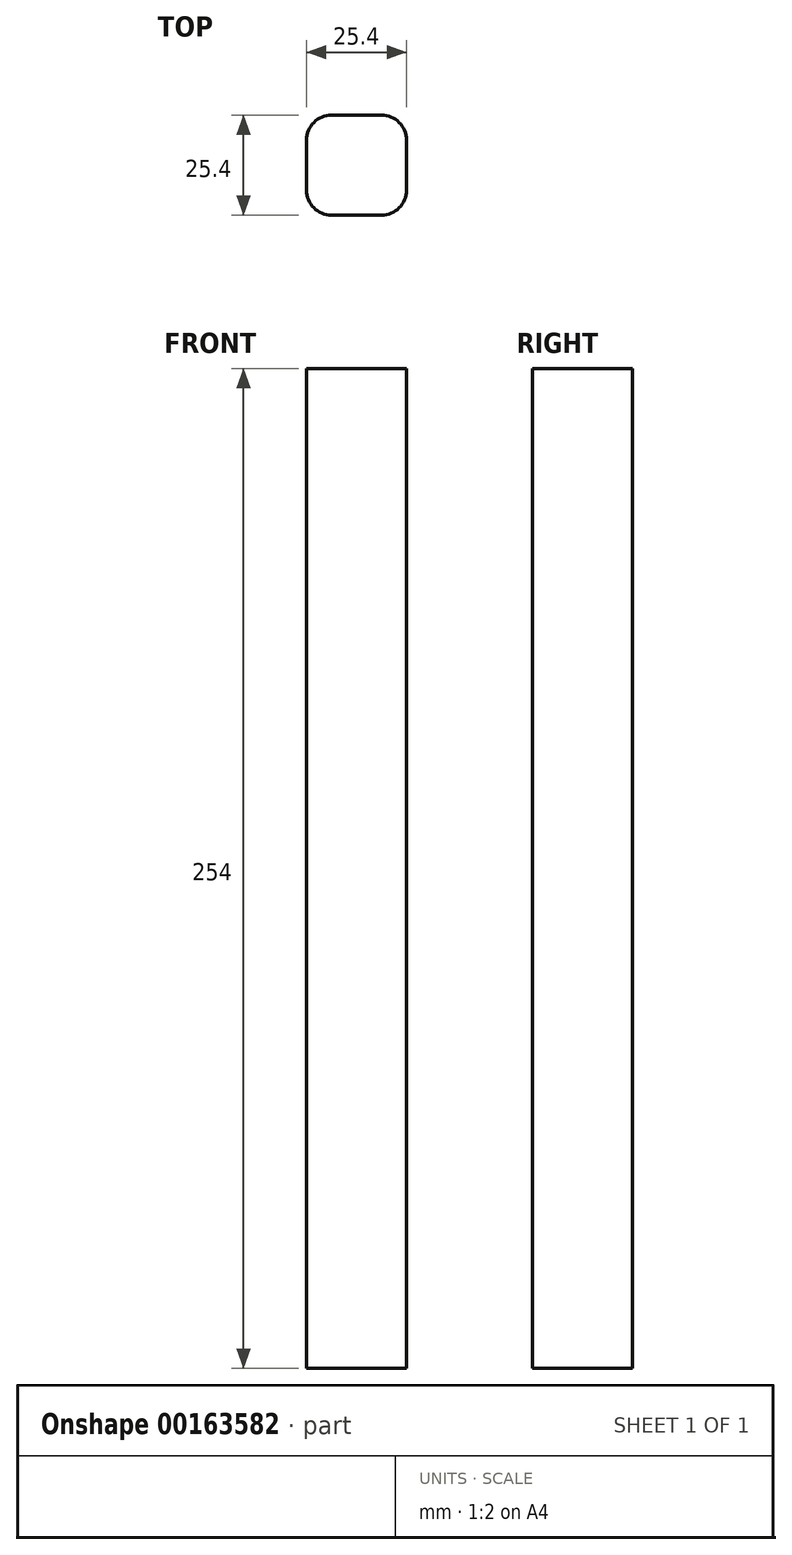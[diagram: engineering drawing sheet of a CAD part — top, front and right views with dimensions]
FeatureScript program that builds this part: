
annotation { "Feature Type Name" : "Feature", "Feature Type Description" : "" }
export const myFeature = defineFeature(function(context is Context, id is Id, definition is map)
    precondition{}
    {
        {
            var Q0;
            Q0=qCreatedBy(makeId("Top.planeOp"),FACE);
            var sketch = newSketch(context, id + "F0", { "sketchPlane" : qUnion([Q0])});
            skLineSegment(sketch, "E0.bottom", {"start": v(6.35, 12.7) * mm, "end": v(-6.35, 12.7) * mm});
            skLineSegment(sketch, "E0.top", {"start": v(6.35, -12.7) * mm, "end": v(-6.35, -12.7) * mm});
            skLineSegment(sketch, "E0.left", {"start": v(12.7, 6.35) * mm, "end": v(12.7, -6.35) * mm});
            skLineSegment(sketch, "E0.right", {"start": v(-12.7, 6.35) * mm, "end": v(-12.7, -6.35) * mm});
            skPoint(sketch, "E0.middle", {"position": v(0, 0) * mm});
            skPoint(sketch, "E1.visualSharp", {"position": v(-12.7, 12.7) * mm});
            skArc(sketch, "E1.filletArc", {"start": v(-6.35, 12.7) * mm, "mid": v(-10.84, 10.84) * mm, "end": v(-12.7, 6.35) * mm});
            skPoint(sketch, "E2.visualSharp", {"position": v(-12.7, -12.7) * mm});
            skArc(sketch, "E2.filletArc", {"start": v(-12.7, -6.35) * mm, "mid": v(-10.84, -10.84) * mm, "end": v(-6.35, -12.7) * mm});
            skPoint(sketch, "E3.visualSharp", {"position": v(12.7, -12.7) * mm});
            skArc(sketch, "E3.filletArc", {"start": v(6.35, -12.7) * mm, "mid": v(10.84, -10.84) * mm, "end": v(12.7, -6.35) * mm});
            skPoint(sketch, "E4.visualSharp", {"position": v(12.7, 12.7) * mm});
            skArc(sketch, "E4.filletArc", {"start": v(12.7, 6.35) * mm, "mid": v(10.84, 10.84) * mm, "end": v(6.35, 12.7) * mm});
            skSolve(sketch);
        }
        {
            var Q0;
            Q0=qSketchRegion(id+"F0",true);
            extrude(context, id + "F1", {"entities" : qUnion([Q0]), "depth" : 254 * mm, "offsetDistance" : 25.4 * mm});
        }
    });
